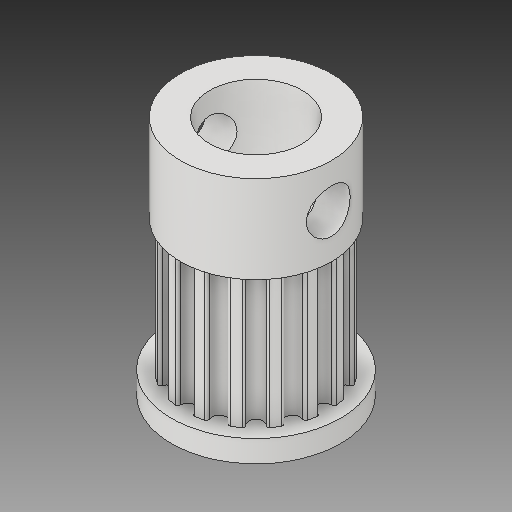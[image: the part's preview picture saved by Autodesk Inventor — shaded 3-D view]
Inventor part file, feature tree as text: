
AUTODESK INVENTOR PART (.ipt)
format: ipt  version: 2018 (Build 220112000, 112)  size: 264,704 bytes
history: native  units: mm
features: extrude x6, sketch x5, pattern_circular x1
ambient origin geometry x8: Origin, YZ Plane, XZ Plane, XY Plane, X Axis, Y Axis, Z Axis, Center Point
bodies: Solid1 (feature_tree)
feature tree (12):
  extrude  "Extrusion1"  Depth=0.5mm
  extrude  "Extrusion2"  Depth=7.0mm TaperAngle=0.0deg
  pattern_circular  "Circular Pattern1"  [2 undecoded]
  extrude  "Extrusion3"  Depth=1.0mm TaperAngle=0.0deg
  sketch  "Sketch4"  dims[d18=6.35mm]
  extrude  "Extrusion4"  Depth=6.0mm TaperAngle=0.0deg
  extrude  "Extrusion5"  Depth=3.0mm
  extrude  "Extrusion6"  Depth=6.0mm TaperAngle=0.0deg
  sketch  "Sketch1"  dims[d8=0.0mm d9=0.5mm]
  sketch  "Sketch2"  dims[d10=0.15mm d12=7.0mm d13=0.0mm]
  sketch  "Sketch3"  dims[d15=360.0deg]
  sketch  "Sketch5"  dims[d20=0.0mm d21=2.0mm d22=1.0mm d23=0.0mm d24=6.0mm d25=0.0mm d26=3.0mm d27=6.0mm d28=0.0mm]
note: 2 required parameter values undecoded (feature->parameter linkage not recoverable at this tier; creation-order binding heuristic only, values carry confidence <= 0.55)
